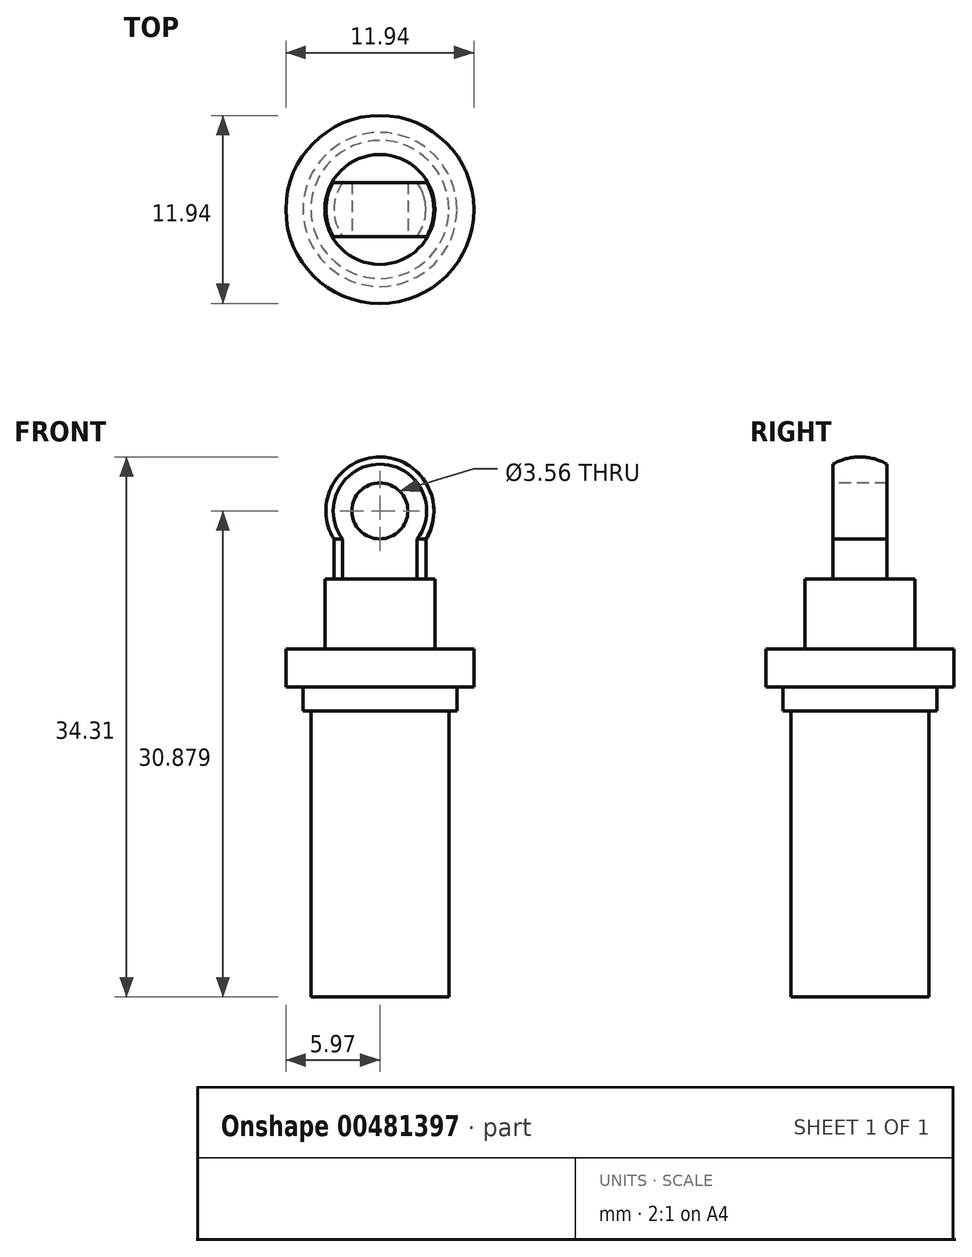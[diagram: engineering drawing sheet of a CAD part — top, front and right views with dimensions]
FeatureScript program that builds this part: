
annotation { "Feature Type Name" : "Feature", "Feature Type Description" : "" }
export const myFeature = defineFeature(function(context is Context, id is Id, definition is map)
    precondition{}
    {
        {
            var Q0;
            Q0=qCreatedBy(makeId("Front.planeOp"),FACE);
            var sketch = newSketch(context, id + "F0", { "sketchPlane" : qUnion([Q0])});
            skLineSegment(sketch, "E0", {"start": v(0, 0) * mm, "end": v(0, 26.54) * mm});
            skLineSegment(sketch, "E1", {"start": v(2.92, 26.54) * mm, "end": v(3.5, 26.54) * mm});
            skLineSegment(sketch, "E2", {"start": v(5.97, 22.1) * mm, "end": v(5.97, 20.83) * mm});
            skLineSegment(sketch, "E3", {"start": v(4.38, 18.16) * mm, "end": v(4.38, 0) * mm});
            skLineSegment(sketch, "E4", {"start": v(2.92, 26.54) * mm, "end": v(2.92, 29.08) * mm});
            skArc(sketch, "E5", {"start": v(2.92, 29.08) * mm, "mid": v(3, 32.55) * mm, "end": v(0, 34.3) * mm});
            skPoint(sketch, "E6.orphan", {"position": v(0, 29.74) * mm});
            skLineSegment(sketch, "E7", {"start": v(0, 34.3) * mm, "end": v(0, 26.54) * mm});
            skLineSegment(sketch, "E8", {"start": v(0, 57.72) * mm, "end": v(0, 0) * mm, "construction": true});
            skLineSegment(sketch, "E9", {"start": v(5.97, 20.83) * mm, "end": v(5.97, 19.68) * mm});
            skLineSegment(sketch, "E10", {"start": v(5.97, 19.68) * mm, "end": v(4.89, 19.68) * mm});
            skLineSegment(sketch, "E11", {"start": v(4.89, 19.68) * mm, "end": v(4.89, 18.16) * mm});
            skLineSegment(sketch, "E12", {"start": v(4.89, 18.16) * mm, "end": v(4.38, 18.16) * mm});
            skLineSegment(sketch, "E13", {"start": v(4.38, 0) * mm, "end": v(0, 0) * mm});
            skLineSegment(sketch, "E14.trimOffspring", {"start": v(0, 0) * mm, "end": v(0, -8.37) * mm, "construction": true});
            skLineSegment(sketch, "E15", {"start": v(3.5, 26.54) * mm, "end": v(3.5, 22.1) * mm});
            skLineSegment(sketch, "E16", {"start": v(3.5, 22.1) * mm, "end": v(5.97, 22.1) * mm});
            skSolve(sketch);
        }
        {
            var Q0;
            Q0 = qSketchRegion(id + "F0", true);
            var Q1;
            Q1=sQuery(id+"F0.wireOp",EDGE,"E8");
            revolve(context, id + "F1", {"entities" : qUnion([Q0]), "axis" : qUnion([Q1]), "revolveType" : RevolveType.FULL});
        }
        {
            var Q0;
            Q0=qCreatedBy(makeId("Right.planeOp"),FACE);
            var sketch = newSketch(context, id + "F2", { "sketchPlane" : qUnion([Q0])});
            skLineSegment(sketch, "E17", {"start": v(-1.71, 26.54) * mm, "end": v(-1.71, 36.7) * mm});
            skLineSegment(sketch, "E18", {"start": v(-1.71, 36.7) * mm, "end": v(-6.16, 36.7) * mm});
            skLineSegment(sketch, "E19", {"start": v(-6.16, 26.54) * mm, "end": v(-6.16, 36.7) * mm});
            skLineSegment(sketch, "E20.0", {"start": v(-3.5, 26.54) * mm, "end": v(-1.71, 26.54) * mm});
            skLineSegment(sketch, "E21", {"start": v(-3.5, 26.54) * mm, "end": v(-6.16, 26.54) * mm});
            skLineSegment(sketch, "E22", {"start": v(0, 39.82) * mm, "end": v(0, 0) * mm, "construction": true});
            skLineSegment(sketch, "E23.MirrorCS", {"start": v(6.16, 26.54) * mm, "end": v(6.16, 36.7) * mm});
            skLineSegment(sketch, "E24.MirrorCS", {"start": v(1.71, 36.7) * mm, "end": v(6.16, 36.7) * mm});
            skLineSegment(sketch, "E25.MirrorCS", {"start": v(1.71, 26.54) * mm, "end": v(1.71, 36.7) * mm});
            skLineSegment(sketch, "E26.MirrorCS", {"start": v(3.5, 26.54) * mm, "end": v(1.71, 26.54) * mm});
            skLineSegment(sketch, "E27.MirrorCS", {"start": v(3.5, 26.54) * mm, "end": v(6.16, 26.54) * mm});
            skSolve(sketch);
        }
        {
            var Q0;
            Q0 = qSketchRegion(id + "F2", true);
            extrude(context, id + "F3", {"entities" : qUnion([Q0]), "operationType" : NewBodyOperationType.REMOVE, "endBound" : BoundingType.THROUGH_ALL, "depth" : 25.4 * mm, "hasSecondDirection" : true, "secondDirectionBound" : SecondDirectionBoundingType.THROUGH_ALL, "secondDirectionOppositeDirection" : true, "secondDirectionDepth" : 25.4 * mm});
        }
        {
            var Q0;
            Q0=qCreatedBy(makeId("Front.planeOp"),FACE);
            var sketch = newSketch(context, id + "F4", { "sketchPlane" : qUnion([Q0])});
            skArc(sketch, "E28.0", {"start": v(2.36, 29.08) * mm, "mid": v(0, 33.85) * mm, "end": v(-2.36, 29.08) * mm, "construction": true});
            skCircle(sketch, "E29", {"center": v(0, 30.88) * mm, "radius": 1.78 * mm});
            skSolve(sketch);
        }
        {
            var Q0;
            Q0 = qSketchRegion(id + "F4", true);
            extrude(context, id + "F5", {"entities" : qUnion([Q0]), "operationType" : NewBodyOperationType.REMOVE, "endBound" : BoundingType.THROUGH_ALL, "oppositeDirection" : true, "depth" : 25.4 * mm, "hasSecondDirection" : true, "secondDirectionBound" : SecondDirectionBoundingType.THROUGH_ALL, "secondDirectionOppositeDirection" : false, "secondDirectionDepth" : 25.4 * mm});
        }
    });
